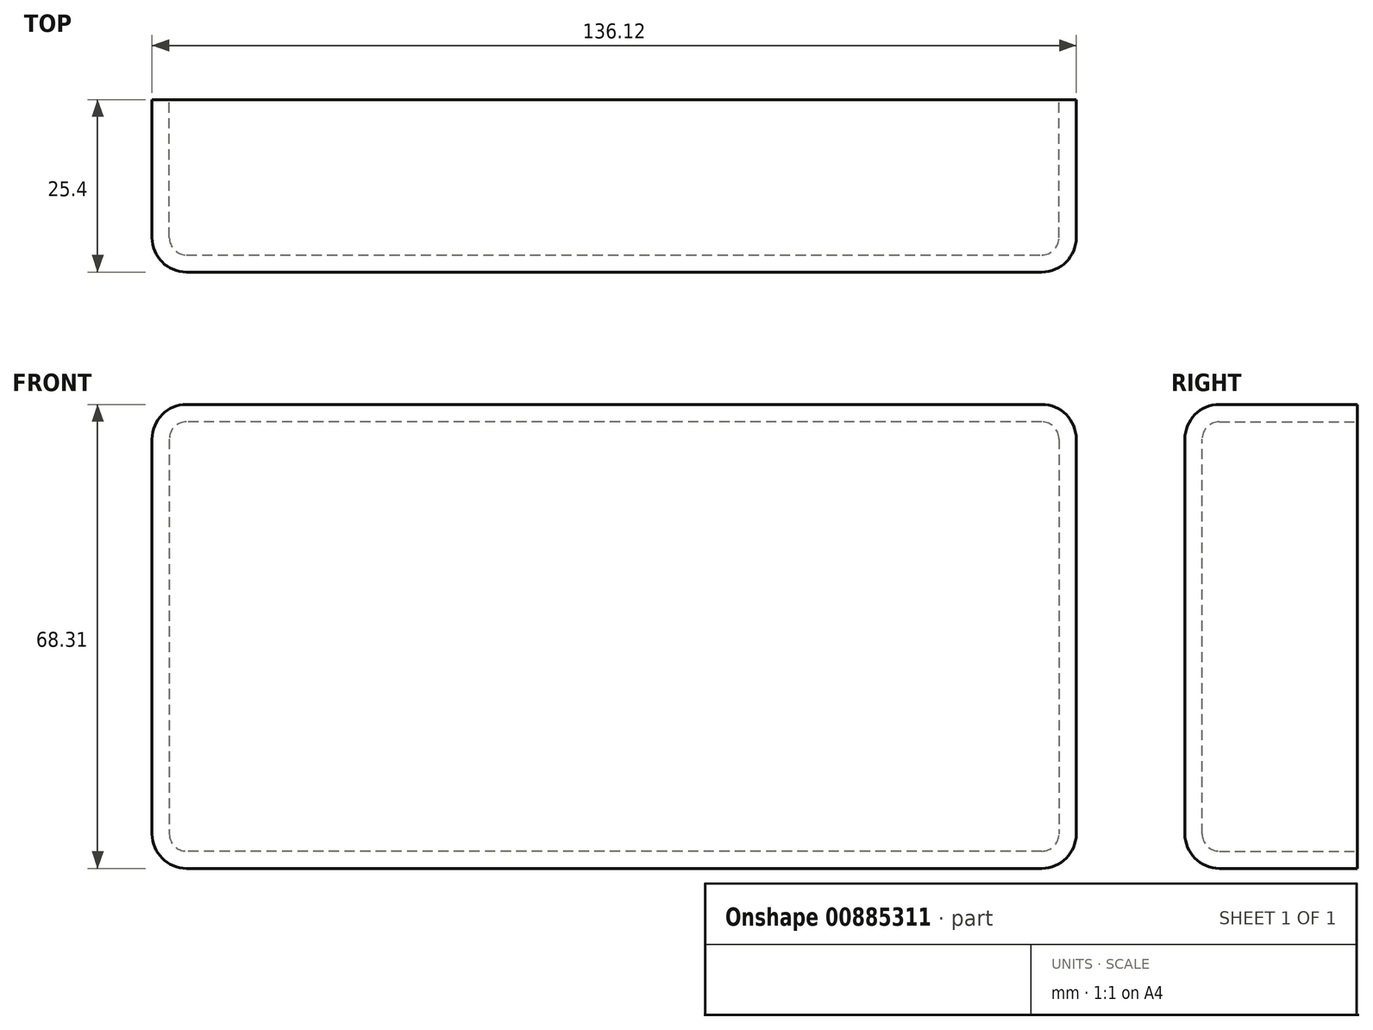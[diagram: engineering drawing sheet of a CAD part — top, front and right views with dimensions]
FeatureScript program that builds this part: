
annotation { "Feature Type Name" : "Feature", "Feature Type Description" : "" }
export const myFeature = defineFeature(function(context is Context, id is Id, definition is map)
    precondition{}
    {
        {
            var Q0;
            Q0=qCreatedBy(makeId("Front.planeOp"),FACE);
            var sketch = newSketch(context, id + "F0", { "sketchPlane" : qUnion([Q0])});
            skLineSegment(sketch, "E0.bottom", {"start": v(55.9, 15.28) * mm, "end": v(-80.22, 15.28) * mm});
            skLineSegment(sketch, "E0.top", {"start": v(55.9, -53.03) * mm, "end": v(-80.22, -53.03) * mm});
            skLineSegment(sketch, "E0.left", {"start": v(55.9, 15.28) * mm, "end": v(55.9, -53.03) * mm});
            skLineSegment(sketch, "E0.right", {"start": v(-80.22, 15.28) * mm, "end": v(-80.22, -53.03) * mm});
            skSolve(sketch);
        }
        {
            var Q0;
            Q0=makeQuery(id+"F0.imprint","IMPRINT",FACE,{"disambiguationData":[TD([[makeQuery(id+"F0.imprint","IMPRINT",EDGE,{"derivedFrom":sQuery(id+"F0.wireOp",EDGE,"E0.bottom")}),1.0]])]});
            var Q1;
            Q1=sQuery(id+"F0.wireOp",EDGE,"E0.right");
            var Q2;
            Q2=sQuery(id+"F0.wireOp",EDGE,"E0.top");
            var Q3;
            Q3=sQuery(id+"F0.wireOp",EDGE,"E0.bottom");
            var Q4;
            Q4=sQuery(id+"F0.wireOp",EDGE,"E0.left");
            extrude(context, id + "F1", {"entities" : qUnion([Q0]), "surfaceEntities" : qUnion([Q1, Q2, Q3, Q4]), "depth" : 25.4 * mm, "offsetDistance" : 25.4 * mm});
        }
        {
            var Q0;
            Q0=makeQuery(id+"F1.opExtrude","SWEPT_EDGE",EDGE,{"disambiguationData":[OSD([sQuery(id+"F0.wireOp",EDGE,"E0.bottom"),sQuery(id+"F0.wireOp",EDGE,"E0.right")])]});
            var Q1;
            Q1=makeQuery(id+"F1.opExtrude","SWEPT_EDGE",EDGE,{"disambiguationData":[OSD([sQuery(id+"F0.wireOp",EDGE,"E0.bottom"),sQuery(id+"F0.wireOp",EDGE,"E0.left")])]});
            var Q2;
            Q2=makeQuery(id+"F1.opExtrude","SWEPT_EDGE",EDGE,{"disambiguationData":[OSD([sQuery(id+"F0.wireOp",EDGE,"E0.top"),sQuery(id+"F0.wireOp",EDGE,"E0.right")])]});
            var Q3;
            Q3=makeQuery(id+"F1.opExtrude","SWEPT_EDGE",EDGE,{"disambiguationData":[OSD([sQuery(id+"F0.wireOp",EDGE,"E0.top"),sQuery(id+"F0.wireOp",EDGE,"E0.left")])]});
            fillet(context, id + "F2", {"entities" : qUnion([Q0, Q1, Q2, Q3]), "radius" : 5.08 * mm, "tangentPropagation" : true, "allowEdgeOverflow" : false});
        }
        {
            var Q0;
            Q0=makeQuery(id+"F1.opExtrude","CAP_EDGE",EDGE,{"disambiguationData":[OSD([sQuery(id+"F0.wireOp",EDGE,"E0.right")])],"isStart":false});
            fillet(context, id + "F3", {"entities" : qUnion([Q0]), "radius" : 5.08 * mm, "tangentPropagation" : true, "allowEdgeOverflow" : false});
        }
        {
            var Q0;
            Q0=makeQuery(id+"F1.opExtrude","CAP_FACE",FACE,{"disambiguationData":[OSD([sQuery(id+"F0.wireOp",EDGE,"E0.bottom"),sQuery(id+"F0.wireOp",EDGE,"E0.top"),sQuery(id+"F0.wireOp",EDGE,"E0.left"),sQuery(id+"F0.wireOp",EDGE,"E0.right")])],"isStart":true});
            shell(context, id + "F4", {"entities" : qUnion([Q0]), "thickness" : 2.54 * mm});
        }
    });
